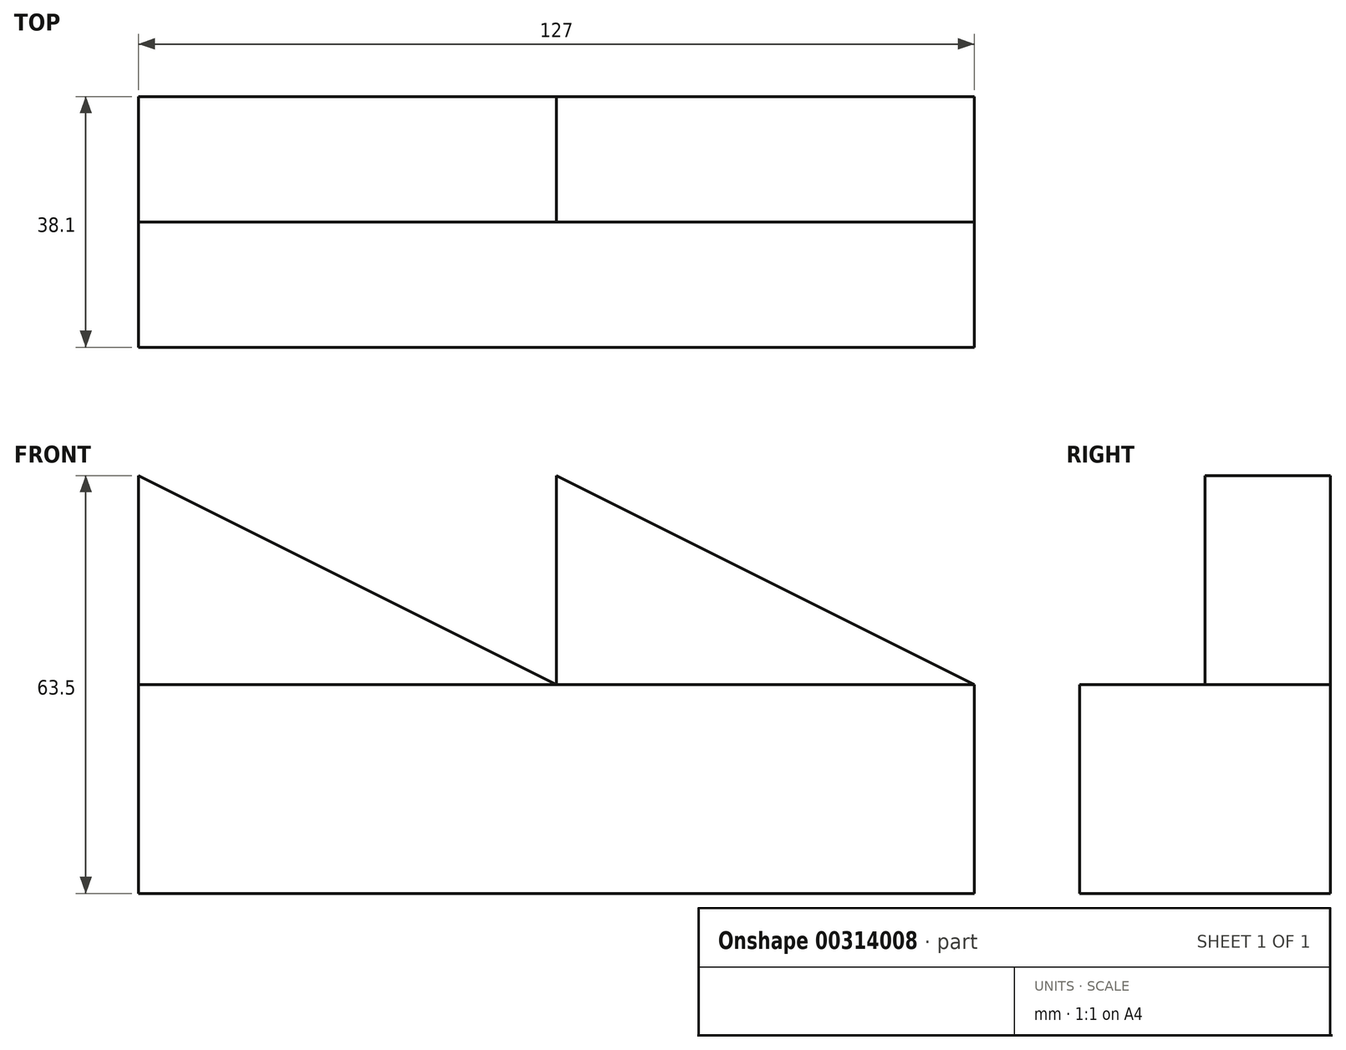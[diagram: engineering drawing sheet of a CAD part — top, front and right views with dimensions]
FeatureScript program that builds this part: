
annotation { "Feature Type Name" : "Feature", "Feature Type Description" : "" }
export const myFeature = defineFeature(function(context is Context, id is Id, definition is map)
    precondition{}
    {
        {
            var Q0;
            Q0=qCreatedBy(makeId("Front.planeOp"),FACE);
            var sketch = newSketch(context, id + "F0", { "sketchPlane" : qUnion([Q0])});
            skLineSegment(sketch, "E0", {"start": v(-31.75, 16.04) * mm, "end": v(31.75, 16.04) * mm});
            skLineSegment(sketch, "E1", {"start": v(-31.75, 16.04) * mm, "end": v(-31.75, 47.8) * mm});
            skLineSegment(sketch, "E2", {"start": v(-31.75, 47.8) * mm, "end": v(31.75, 16.04) * mm});
            skLineSegment(sketch, "E3", {"start": v(31.75, 16.04) * mm, "end": v(95.25, 16.04) * mm});
            skLineSegment(sketch, "E4", {"start": v(31.75, 16.04) * mm, "end": v(31.75, 47.8) * mm});
            skLineSegment(sketch, "E5", {"start": v(31.75, 47.8) * mm, "end": v(95.25, 16.04) * mm});
            skLineSegment(sketch, "E6", {"start": v(-31.75, 16.04) * mm, "end": v(-31.75, -15.7) * mm});
            skLineSegment(sketch, "E7", {"start": v(-31.75, -15.7) * mm, "end": v(95.25, -15.7) * mm});
            skLineSegment(sketch, "E8", {"start": v(95.25, 16.04) * mm, "end": v(95.25, -15.7) * mm});
            skSolve(sketch);
        }
        {
            var Q0;
            Q0=makeQuery(id+"F0.imprint","IMPRINT",FACE,{"disambiguationData":[TD([[makeQuery(id+"F0.imprint","IMPRINT",EDGE,{"derivedFrom":sQuery(id+"F0.wireOp",EDGE,"E0")}),-1.0]])]});
            extrude(context, id + "F1", {"entities" : qUnion([Q0]), "depth" : 38.1 * mm});
        }
        {
            var Q0;
            Q0 = qSketchRegion(id + "F0", true);
            extrude(context, id + "F2", {"entities" : qUnion([Q0]), "operationType" : NewBodyOperationType.ADD, "depth" : 19.05 * mm});
        }
    });
